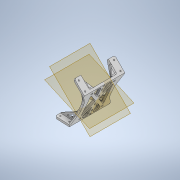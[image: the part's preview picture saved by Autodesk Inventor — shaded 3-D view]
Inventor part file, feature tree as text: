
AUTODESK INVENTOR PART (.ipt)
format: ipt  version: 2020 (Build 240168000, 168)  size: 826,368 bytes
history: native  units: mm
features: sketch x1
bodies: Body1 (feature_tree)
feature tree (1):
  sketch  "Sketch12"  dims[d1=3.0mm d2=22.0mm d4=3.0mm d5=22.0mm d6=10.0mm d7=0.0mm d8=2.0mm d9=6.0mm d10=4.0mm d11=2.0mm d12=90.0deg d13=20.0mm d14=0.0mm d15=2.0mm d16=6.0mm d17=4.0mm d18=2.0mm d19=90.0deg d20=20.0mm d21=0.0mm d22=3.0mm d23=10.0mm d24=0.0mm d25=10.0mm d26=10.0mm d27=2.0mm d28=0.0mm d29=2.0mm d30=0.0mm d31=10.0mm d32=10.0mm d33=15.0mm d34=15.0mm d35=2.0mm d36=0.0mm d37=2.0mm d38=2.0mm d39=45.0deg d40=2.0mm d41=2.5mm d42=2.5mm d43=2.5mm d44=2.5mm d45=2.5mm d46=2.5mm d47=500.0mm d48=0.0mm d49=0.7mm d50=2.0mm d51=20.0mm d52=2.0mm d53=2.0mm d54=4.0mm d55=7.0mm d56=4.0mm d57=7.0mm d58=3.0mm d59=3.0mm d60=3.0mm d61=3.0mm d62=500.0mm d63=0.0mm d64=35.0mm d65=47.0mm d66=3.0mm d67=3.0mm d68=3.0mm d69=3.0mm d70=20.0mm d71=0.0mm d72=4.0mm d73=2.0mm d74=2.0mm d75=2.0mm d76=2.0mm d78=4.0mm d79=2.0mm d80=1.0mm d81=20.0mm d82=0.0mm d83=30.0deg d84=4.0mm d85=4.0mm d86=4.0mm d87=1.0mm d88=2.0mm d89=20.0mm d90=0.0mm d91=12.0mm d92=12.0mm d93=3.0mm d94=3.0mm d95=20.0mm d96=0.0mm]
